# Revit family: 201_NOT-S-_
name_source: partatom
category: Air Terminals
units: mm (PartAtom-declared; Revit-internal decimal feet)

## family parameters
Always vertical = Yes
Cut with Voids When Loaded = No
Part Type = Normal
Room Calculation Point = Yes
Round Connector Dimension = Use Diameter
Shared = No
Work Plane-Based = No

## types (5) — shared parameters
CAT0 = Yes
CL_Location_5000 = 5000 mm  [stored 16.4042 ft]
Description = Supply air diffuser
L_ARR = 400 mm  [stored 1.31234 ft]
Manufacturer = Climecon
QmdConnectorList = 201;D
URL = www.climecon.fi
W_ARR = 400 mm  [stored 1.31234 ft]
XRefLineVPlnId = 7453
YRefLineVPlnId = 7456
magiPartTypeId = 201
magiProductFamilyId = NOT-S-*
zero-valued in all types: CLBTZ, H_ARR, MC_Default_elevation

## per-type parameters (varying)
| type | A | B | B__ve | C1 | C1__ve | D | R | Z1 |
| NOT-S-125 | 386 mm  [stored 1.2664 ft] | 205 mm  [stored 0.672572 ft] | -205 mm  [stored -0.672572 ft] | 1738 mm  [stored 5.7021 ft] | -1738 mm  [stored -5.7021 ft] | 125 mm | 63 mm | 103 mm |
| NOT-S-315 | 638 mm  [stored 2.09318 ft] | 395 mm  [stored 1.29593 ft] | -395 mm  [stored -1.29593 ft] | 1864 mm  [stored 6.11549 ft] | -1864 mm  [stored -6.11549 ft] | 315 mm | 158 mm | 198 mm |
| NOT-S-250 | 638 mm  [stored 2.09318 ft] | 330 mm  [stored 1.08268 ft] | -330 mm  [stored -1.08268 ft] | 1864 mm  [stored 6.11549 ft] | -1864 mm  [stored -6.11549 ft] | 250 mm | 125 mm  [stored 0.410105 ft] | 165 mm  [stored 0.541339 ft] |
| NOT-S-200 | 580 mm  [stored 1.90289 ft] | 280 mm  [stored 0.918635 ft] | -280 mm  [stored -0.918635 ft] | 1835 mm  [stored 6.02034 ft] | -1835 mm  [stored -6.02034 ft] | 200 mm | 100 mm  [stored 0.328084 ft] | 140 mm  [stored 0.459318 ft] |
| NOT-S-160 | 475 mm  [stored 1.5584 ft] | 240 mm  [stored 0.787402 ft] | -240 mm  [stored -0.787402 ft] | 1783 mm | -1783 mm | 160 mm | 80 mm  [stored 0.262467 ft] | 120 mm  [stored 0.393701 ft] |

note: column(s) folded — value = type name in every type: magiProductCode, magiProductId

note: [stored X ft] marks values corroborated as IEEE doubles in the binary element streams (Revit-internal decimal feet)

## geometry (parser evidence)
native form markers: Sweep x2
no freeform markers — native parametric forms only
